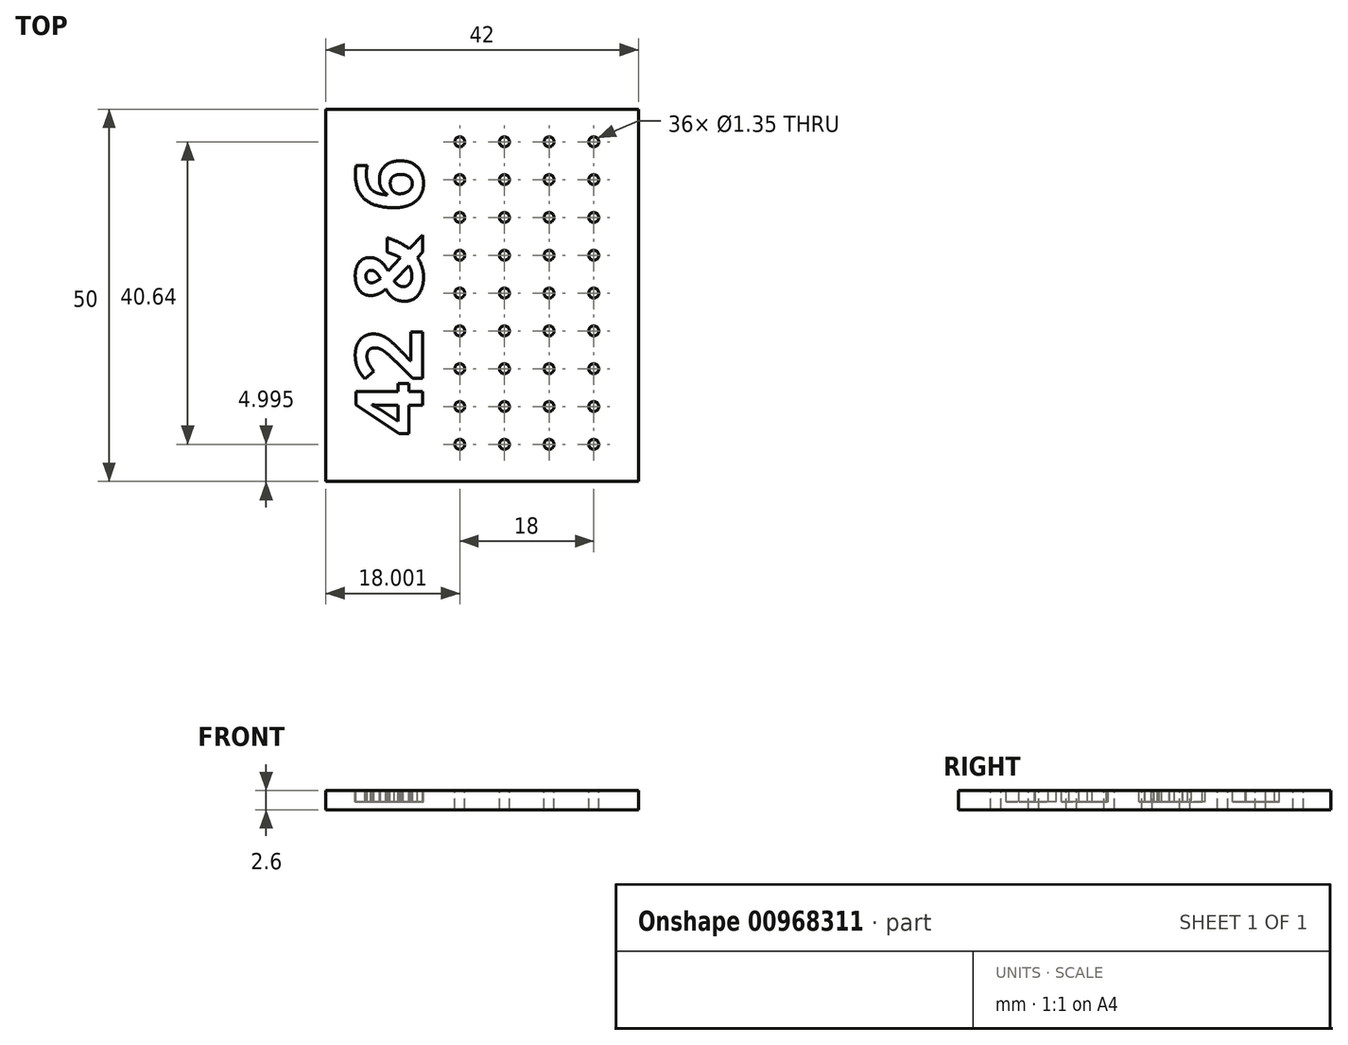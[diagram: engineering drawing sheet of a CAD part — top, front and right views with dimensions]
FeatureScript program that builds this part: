
annotation { "Feature Type Name" : "Feature", "Feature Type Description" : "" }
export const myFeature = defineFeature(function(context is Context, id is Id, definition is map)
    precondition{}
    {
        {
            var Q0;
            Q0=qCreatedBy(makeId("Top.planeOp"),FACE);
            var sketch = newSketch(context, id + "F0", { "sketchPlane" : qUnion([Q0])});
            skLineSegment(sketch, "E0.bottom", {"start": v(-43.16, 28.34) * mm, "end": v(-1.16, 28.34) * mm});
            skLineSegment(sketch, "E0.top", {"start": v(-43.16, -21.66) * mm, "end": v(-1.16, -21.66) * mm});
            skLineSegment(sketch, "E0.left", {"start": v(-43.16, 28.34) * mm, "end": v(-43.16, -21.66) * mm});
            skLineSegment(sketch, "E0.right", {"start": v(-1.16, 28.34) * mm, "end": v(-1.16, -21.66) * mm});
            skSolve(sketch);
        }
        {
            var Q0;
            Q0=makeQuery(id+"F0.imprint","IMPRINT",FACE,{"disambiguationData":[TD([[makeQuery(id+"F0.imprint","IMPRINT",EDGE,{"derivedFrom":sQuery(id+"F0.wireOp",EDGE,"E0.bottom")}),-1.0]])]});
            extrude(context, id + "F1", {"entities" : qUnion([Q0]), "depth" : 2.6 * mm, "offsetDistance" : 25 * mm});
        }
        {
            var Q0;
            Q0=makeQuery(id+"F1.opExtrude","CAP_FACE",FACE,{"disambiguationData":[OSD([sQuery(id+"F0.wireOp",EDGE,"E0.bottom"),sQuery(id+"F0.wireOp",EDGE,"E0.top"),sQuery(id+"F0.wireOp",EDGE,"E0.left"),sQuery(id+"F0.wireOp",EDGE,"E0.right")])],"isStart":false});
            var sketch = newSketch(context, id + "F2", { "sketchPlane" : qUnion([Q0])});
            skText(sketch, "E1", { "text": "42 & 6", "fontName": "OpenSans-Bold.ttf"});
            const initialGuessF2  = {"E1": [-0.03016, -0.01546, 0, 1, 0.009]};
            skSetInitialGuess(sketch, initialGuessF2);
            skSolve(sketch);
        }
        {
            var Q0;
            Q0=qSketchRegion(id+"F2",true);
            extrude(context, id + "F3", {"entities" : qUnion([Q0]), "operationType" : NewBodyOperationType.REMOVE, "oppositeDirection" : true, "depth" : 1.5 * mm, "offsetDistance" : 25 * mm});
        }
        {
            var Q0;
            {var subQ0=sQuery(id+"F0.wireOp",EDGE,"E0.left");var subQ1=sQuery(id+"F0.wireOp",EDGE,"E0.bottom");var subQ2=sQuery(id+"F0.wireOp",EDGE,"E0.right");var subQ3=sQuery(id+"F0.wireOp",EDGE,"E0.top");Q0=makeQuery(id+"F3.boolean.opBoolean","SPLIT",FACE,{"disambiguationData":[TD([makeQuery(id+"F1.opExtrude","SWEPT_FACE",FACE,{"disambiguationData":[OSD([subQ1])]})])],"derivedFrom":makeQuery(id+"F1.opExtrude","CAP_FACE",FACE,{"disambiguationData":[OSD([subQ1,subQ3,subQ0,subQ2])],"isStart":false})});}
            var sketch = newSketch(context, id + "F4", { "sketchPlane" : qUnion([Q0])});
            skCircle(sketch, "E2", {"center": v(-25.16, -16.66) * mm, "radius": 0.68 * mm});
            skCircle(sketch, "E3", {"center": v(-25.16, -11.58) * mm, "radius": 0.68 * mm});
            skCircle(sketch, "E4", {"center": v(-25.16, -6.5) * mm, "radius": 0.68 * mm});
            skCircle(sketch, "E5", {"center": v(-25.16, -1.42) * mm, "radius": 0.68 * mm});
            skCircle(sketch, "E6", {"center": v(-25.16, 3.66) * mm, "radius": 0.68 * mm});
            skCircle(sketch, "E7", {"center": v(-25.16, 8.74) * mm, "radius": 0.68 * mm});
            skCircle(sketch, "E8", {"center": v(-25.16, 13.82) * mm, "radius": 0.68 * mm});
            skCircle(sketch, "E9", {"center": v(-25.16, 18.9) * mm, "radius": 0.68 * mm});
            skCircle(sketch, "E10", {"center": v(-19.16, -16.66) * mm, "radius": 0.68 * mm});
            skCircle(sketch, "E11", {"center": v(-19.16, -11.58) * mm, "radius": 0.68 * mm});
            skCircle(sketch, "E12", {"center": v(-19.16, -6.5) * mm, "radius": 0.68 * mm});
            skCircle(sketch, "E13", {"center": v(-19.16, -1.42) * mm, "radius": 0.68 * mm});
            skCircle(sketch, "E14", {"center": v(-19.16, 3.66) * mm, "radius": 0.68 * mm});
            skCircle(sketch, "E15", {"center": v(-19.16, 8.74) * mm, "radius": 0.68 * mm});
            skCircle(sketch, "E16", {"center": v(-19.16, 13.82) * mm, "radius": 0.68 * mm});
            skCircle(sketch, "E17", {"center": v(-19.16, 18.9) * mm, "radius": 0.68 * mm});
            skCircle(sketch, "E18", {"center": v(-13.16, -16.66) * mm, "radius": 0.68 * mm});
            skCircle(sketch, "E19", {"center": v(-13.16, -11.58) * mm, "radius": 0.68 * mm});
            skCircle(sketch, "E20", {"center": v(-13.16, -6.5) * mm, "radius": 0.68 * mm});
            skCircle(sketch, "E21", {"center": v(-13.16, -1.42) * mm, "radius": 0.68 * mm});
            skCircle(sketch, "E22", {"center": v(-13.16, 3.66) * mm, "radius": 0.68 * mm});
            skCircle(sketch, "E23", {"center": v(-13.16, 8.74) * mm, "radius": 0.68 * mm});
            skCircle(sketch, "E24", {"center": v(-13.16, 13.82) * mm, "radius": 0.68 * mm});
            skCircle(sketch, "E25", {"center": v(-13.16, 18.9) * mm, "radius": 0.68 * mm});
            skCircle(sketch, "E26", {"center": v(-25.16, 23.98) * mm, "radius": 0.68 * mm});
            skCircle(sketch, "E27", {"center": v(-19.16, 23.98) * mm, "radius": 0.68 * mm});
            skCircle(sketch, "E28", {"center": v(-13.16, 23.98) * mm, "radius": 0.68 * mm});
            skCircle(sketch, "E29", {"center": v(-7.16, -16.66) * mm, "radius": 0.68 * mm});
            skCircle(sketch, "E30", {"center": v(-7.16, -11.58) * mm, "radius": 0.68 * mm});
            skCircle(sketch, "E31", {"center": v(-7.16, -6.5) * mm, "radius": 0.68 * mm});
            skCircle(sketch, "E32", {"center": v(-7.16, -1.42) * mm, "radius": 0.68 * mm});
            skCircle(sketch, "E33", {"center": v(-7.16, 3.66) * mm, "radius": 0.68 * mm});
            skCircle(sketch, "E34", {"center": v(-7.16, 8.74) * mm, "radius": 0.68 * mm});
            skCircle(sketch, "E35", {"center": v(-7.16, 13.82) * mm, "radius": 0.68 * mm});
            skCircle(sketch, "E36", {"center": v(-7.16, 18.9) * mm, "radius": 0.68 * mm});
            skCircle(sketch, "E37", {"center": v(-7.16, 23.98) * mm, "radius": 0.68 * mm});
            skSolve(sketch);
        }
        {
            var Q0;
            Q0 = qSketchRegion(id + "F4", true);
            extrude(context, id + "F5", {"entities" : qUnion([Q0]), "operationType" : NewBodyOperationType.REMOVE, "endBound" : BoundingType.UP_TO_NEXT, "oppositeDirection" : true, "depth" : 25 * mm, "offsetDistance" : 25 * mm});
        }
    });
